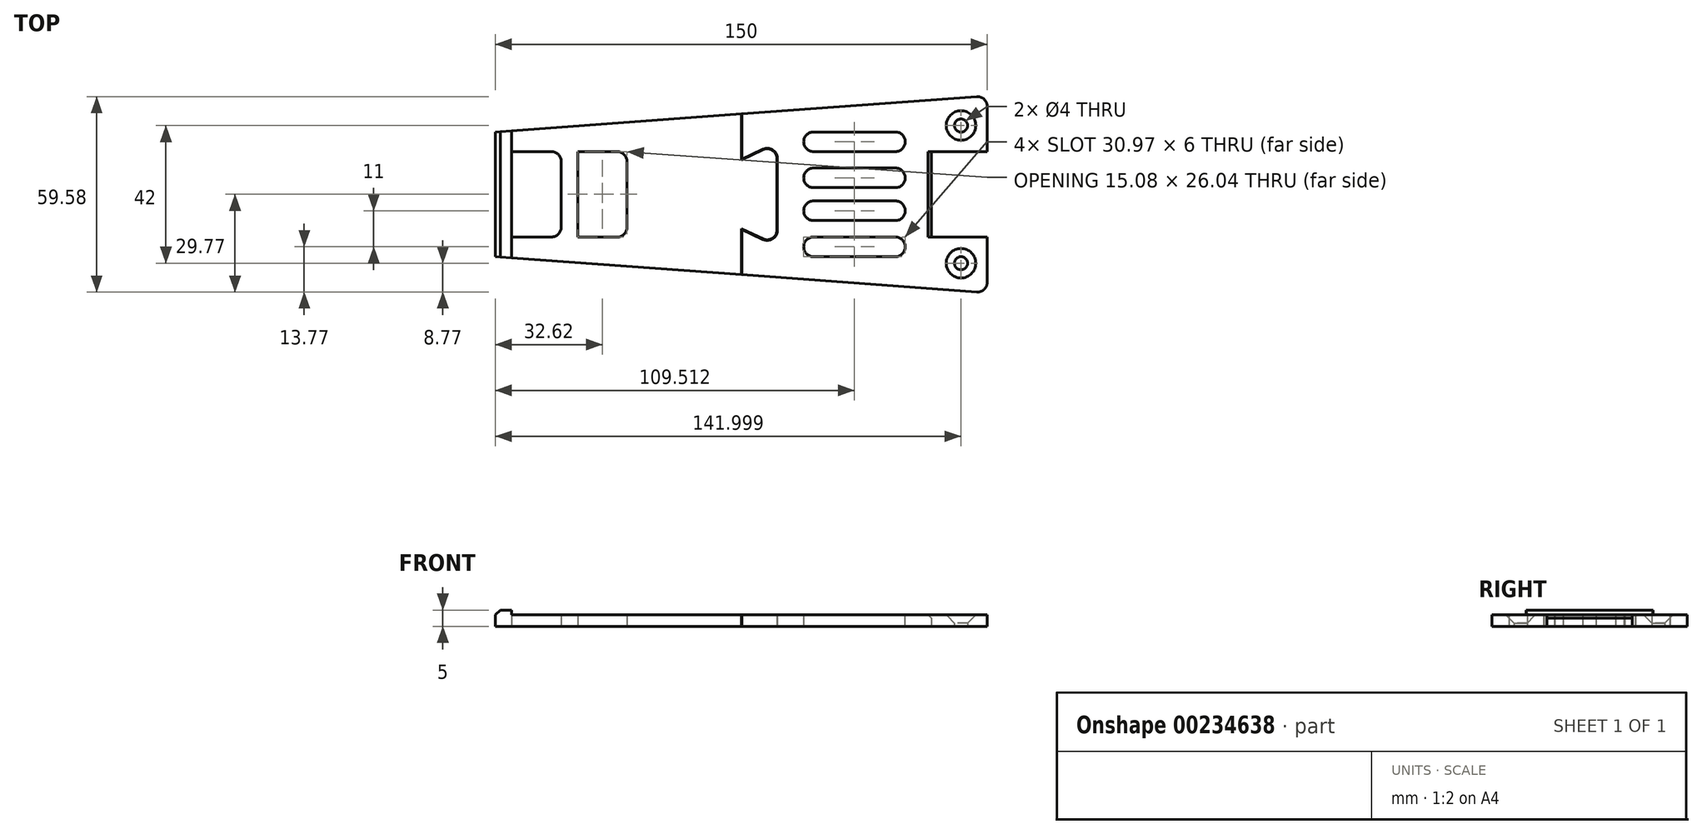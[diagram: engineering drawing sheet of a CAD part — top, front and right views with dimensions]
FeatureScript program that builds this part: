
annotation { "Feature Type Name" : "Feature", "Feature Type Description" : "" }
export const myFeature = defineFeature(function(context is Context, id is Id, definition is map)
    precondition{}
    {
        {
            var Q0;
            Q0=qCreatedBy(makeId("Top.planeOp"),FACE);
            var sketch = newSketch(context, id + "F0", { "sketchPlane" : qUnion([Q0])});
            skLineSegment(sketch, "E0.left", {"start": v(80.65, -28) * mm, "end": v(80.65, -11) * mm});
            skPoint(sketch, "E0.middle", {"position": v(0, 0) * mm});
            skLineSegment(sketch, "E1.trimOffspring", {"start": v(80.65, 15.04) * mm, "end": v(80.65, 32.04) * mm});
            skCircle(sketch, "E2", {"center": v(72.65, 23) * mm, "radius": 2 * mm});
            skCircle(sketch, "E3.MirrorC", {"center": v(72.65, -19) * mm, "radius": 2 * mm});
            skLineSegment(sketch, "E4", {"start": v(63.65, 15.04) * mm, "end": v(63.65, -11) * mm});
            skLineSegment(sketch, "E5", {"start": v(-49.27, -11) * mm, "end": v(-49.27, 15.04) * mm});
            skLineSegment(sketch, "E6", {"start": v(80.65, 15.04) * mm, "end": v(63.65, 15.04) * mm});
            skLineSegment(sketch, "E7", {"start": v(80.65, -11) * mm, "end": v(63.65, -11) * mm});
            skLineSegment(sketch, "E8", {"start": v(-49.27, 15.04) * mm, "end": v(-64.35, 15.04) * mm});
            skLineSegment(sketch, "E9", {"start": v(-49.27, -11) * mm, "end": v(-64.35, -11) * mm});
            skLineSegment(sketch, "E10", {"start": v(-64.35, -11) * mm, "end": v(-64.35, 15.04) * mm});
            skLineSegment(sketch, "E11", {"start": v(80.65, -28) * mm, "end": v(-69.35, -28) * mm, "construction": true});
            skLineSegment(sketch, "E12", {"start": v(80.65, 32.04) * mm, "end": v(-69.35, 32.04) * mm, "construction": true});
            skLineSegment(sketch, "E13", {"start": v(63.65, 15.04) * mm, "end": v(-49.27, 15.04) * mm, "construction": true});
            skLineSegment(sketch, "E14", {"start": v(-69.35, 32.04) * mm, "end": v(-69.35, 21.04) * mm, "construction": true});
            skLineSegment(sketch, "E15", {"start": v(-69.35, -28) * mm, "end": v(-69.35, -17) * mm, "construction": true});
            skLineSegment(sketch, "E16", {"start": v(-29.2, -11.02) * mm, "end": v(-29.2, 15.02) * mm});
            skLineSegment(sketch, "E17", {"start": v(-29.2, 15.02) * mm, "end": v(-44.27, 15.02) * mm});
            skLineSegment(sketch, "E18", {"start": v(-29.2, -11.02) * mm, "end": v(-44.27, -11.02) * mm});
            skLineSegment(sketch, "E19", {"start": v(-44.27, -11.02) * mm, "end": v(-44.27, 15.02) * mm});
            skLineSegment(sketch, "E20", {"start": v(80.65, 32.04) * mm, "end": v(5.8, 26.55) * mm});
            skLineSegment(sketch, "E21", {"start": v(80.65, -28) * mm, "end": v(5.8, -22.51) * mm});
            skLineSegment(sketch, "E22", {"start": v(-69.35, 21.04) * mm, "end": v(-69.35, -17) * mm});
            skLineSegment(sketch, "E23", {"start": v(5.65, 26.54) * mm, "end": v(5.65, 12.54) * mm});
            skLineSegment(sketch, "E24", {"start": v(5.65, -22.5) * mm, "end": v(5.65, -8.5) * mm});
            skLineSegment(sketch, "E25", {"start": v(5.65, -8.5) * mm, "end": v(12.26, -11.58) * mm});
            skLineSegment(sketch, "E26", {"start": v(16.52, -8.86) * mm, "end": v(16.52, 12.9) * mm});
            skLineSegment(sketch, "E27", {"start": v(5.65, 12.54) * mm, "end": v(12.26, 15.62) * mm});
            skLineSegment(sketch, "E28.trimOffspring", {"start": v(5.65, -8.5) * mm, "end": v(5.65, -22.5) * mm});
            skPoint(sketch, "E29.visualSharp", {"position": v(16.52, 17.6) * mm});
            skArc(sketch, "E29.filletArc", {"start": v(16.52, 12.9) * mm, "mid": v(15.14, 15.43) * mm, "end": v(12.26, 15.62) * mm});
            skPoint(sketch, "E30.visualSharp", {"position": v(16.52, -13.57) * mm});
            skArc(sketch, "E30.filletArc", {"start": v(12.26, -11.58) * mm, "mid": v(15.14, -11.4) * mm, "end": v(16.52, -8.86) * mm});
            skLineSegment(sketch, "E31.0", {"start": v(5.8, -22.51) * mm, "end": v(5.8, -8.74) * mm});
            skLineSegment(sketch, "E31.1", {"start": v(5.8, -8.74) * mm, "end": v(12.2, -11.72) * mm});
            skArc(sketch, "E31.2", {"start": v(12.2, -11.72) * mm, "mid": v(15.22, -11.52) * mm, "end": v(16.67, -8.86) * mm});
            skLineSegment(sketch, "E31.3", {"start": v(5.8, 26.55) * mm, "end": v(5.8, 12.77) * mm});
            skLineSegment(sketch, "E31.4", {"start": v(5.8, 12.77) * mm, "end": v(12.2, 15.75) * mm});
            skArc(sketch, "E31.5", {"start": v(16.67, 12.9) * mm, "mid": v(15.22, 15.56) * mm, "end": v(12.2, 15.75) * mm});
            skLineSegment(sketch, "E31.6", {"start": v(16.67, -8.86) * mm, "end": v(16.67, 12.9) * mm});
            skLineSegment(sketch, "E32.trimOffspring", {"start": v(5.65, -22.5) * mm, "end": v(-69.35, -17) * mm});
            skLineSegment(sketch, "E33.trimOffspring", {"start": v(5.65, 26.54) * mm, "end": v(-69.35, 21.04) * mm});
            skLineSegment(sketch, "E34", {"start": v(63.65, -11) * mm, "end": v(-49.27, -11) * mm, "construction": true});
            skLineSegment(sketch, "E35.bottom", {"start": v(24.67, -11) * mm, "end": v(55.65, -11) * mm});
            skLineSegment(sketch, "E35.top", {"start": v(24.67, -17) * mm, "end": v(55.65, -17) * mm});
            skLineSegment(sketch, "E35.left", {"start": v(24.67, -11) * mm, "end": v(24.67, -17) * mm});
            skLineSegment(sketch, "E35.right", {"start": v(55.65, -11) * mm, "end": v(55.65, -17) * mm});
            skLineSegment(sketch, "E36.bottom", {"start": v(24.67, 10.04) * mm, "end": v(55.65, 10.04) * mm});
            skLineSegment(sketch, "E36.top", {"start": v(24.67, 4.04) * mm, "end": v(55.65, 4.04) * mm});
            skLineSegment(sketch, "E36.left", {"start": v(24.67, 10.04) * mm, "end": v(24.67, 4.04) * mm});
            skLineSegment(sketch, "E36.right", {"start": v(55.65, 10.04) * mm, "end": v(55.65, 4.04) * mm});
            skLineSegment(sketch, "E37.bottom", {"start": v(24.67, 0) * mm, "end": v(55.65, 0) * mm});
            skLineSegment(sketch, "E37.top", {"start": v(24.67, -6) * mm, "end": v(55.65, -6) * mm});
            skLineSegment(sketch, "E37.left", {"start": v(24.67, 0) * mm, "end": v(24.67, -6) * mm});
            skLineSegment(sketch, "E37.right", {"start": v(55.65, 0) * mm, "end": v(55.65, -6) * mm});
            skLineSegment(sketch, "E38.bottom", {"start": v(24.67, 21.04) * mm, "end": v(55.65, 21.04) * mm});
            skLineSegment(sketch, "E38.top", {"start": v(24.67, 15.04) * mm, "end": v(55.65, 15.04) * mm});
            skLineSegment(sketch, "E38.left", {"start": v(24.67, 21.04) * mm, "end": v(24.67, 15.04) * mm});
            skLineSegment(sketch, "E38.right", {"start": v(55.65, 21.04) * mm, "end": v(55.65, 15.04) * mm});
            skSolve(sketch);
        }
        {
            var Q0;
            Q0=makeQuery(id+"F0.imprint","IMPRINT",FACE,{"disambiguationData":[TD([[makeQuery(id+"F0.imprint","IMPRINT",EDGE,{"derivedFrom":sQuery(id+"F0.wireOp",EDGE,"E5")}),-1.0]])]});
            var Q1;
            Q1=makeQuery(id+"F0.imprint","IMPRINT",FACE,{"disambiguationData":[TD([[makeQuery(id+"F0.imprint","IMPRINT",EDGE,{"derivedFrom":sQuery(id+"F0.wireOp",EDGE,"E0.left")}),1.0]])]});
            extrude(context, id + "F1", {"entities" : qUnion([Q0, Q1]), "depth" : 3.5 * mm});
        }
        {
            var Q0;
            {var subQ0=sQuery(id+"F0.wireOp",EDGE,"E4");Q0=makeQuery(id+"F1.opExtrude","CAP_EDGE",EDGE,{"disambiguationData":[OSD([subQ0]),TDD([makeQuery(id+"F0.imprint","IMPRINT",EDGE,{"disambiguationData":[TD([[makeQuery(id+"F0.imprint","INTERSECT",VERTEX,{"derivedFrom":[sQuery(id+"F0.wireOp",EDGE,"a1183fda-915b-4a70-979b-ef1662e096630.MirrorCS"),subQ0]}),-1.0]])],"derivedFrom":subQ0})])],"isStart":false});}
            var Q1;
            {var subQ0=sQuery(id+"F0.wireOp",EDGE,"E4");Q1=makeQuery(id+"F1.opExtrude","CAP_EDGE",EDGE,{"disambiguationData":[OSD([subQ0]),TDD([makeQuery(id+"F0.imprint","IMPRINT",EDGE,{"disambiguationData":[TD([[makeQuery(id+"F0.imprint","INTERSECT",VERTEX,{"derivedFrom":[sQuery(id+"F0.wireOp",EDGE,"irKfdA7U-XoDH-ahAc-nykv-EBvfS3rGnkAg.top"),subQ0]}),1.0]])],"derivedFrom":subQ0})])],"isStart":false});}
            chamfer(context, id + "F2", {"entities" : qUnion([Q0, Q1]), "width" : 1 * mm, "tangentPropagation" : true});
        }
        {
            var Q0;
            Q0=makeQuery(id+"F1.opExtrude","CAP_EDGE",EDGE,{"disambiguationData":[OSD([sQuery(id+"F0.wireOp",EDGE,"E2")])],"isStart":false});
            var Q1;
            Q1=makeQuery(id+"F1.opExtrude","CAP_EDGE",EDGE,{"disambiguationData":[OSD([sQuery(id+"F0.wireOp",EDGE,"E3.MirrorC")])],"isStart":false});
            chamfer(context, id + "F3", {"entities" : qUnion([Q0, Q1]), "width" : 2.5 * mm, "tangentPropagation" : true});
        }
        {
            var Q0;
            Q0=makeQuery(id+"F1.opExtrude","CAP_FACE",FACE,{"disambiguationData":[OSD([sQuery(id+"F0.wireOp",EDGE,"E5"),sQuery(id+"F0.wireOp",EDGE,"E8"),sQuery(id+"F0.wireOp",EDGE,"E9"),sQuery(id+"F0.wireOp",EDGE,"E10"),sQuery(id+"F0.wireOp",EDGE,"E16"),sQuery(id+"F0.wireOp",EDGE,"E17"),sQuery(id+"F0.wireOp",EDGE,"E18"),sQuery(id+"F0.wireOp",EDGE,"E19"),sQuery(id+"F0.wireOp",EDGE,"E22"),sQuery(id+"F0.wireOp",EDGE,"E25"),sQuery(id+"F0.wireOp",EDGE,"E26"),sQuery(id+"F0.wireOp",EDGE,"E23"),sQuery(id+"F0.wireOp",EDGE,"E27"),sQuery(id+"F0.wireOp",EDGE,"E28.trimOffspring"),sQuery(id+"F0.wireOp",EDGE,"E29.filletArc"),sQuery(id+"F0.wireOp",EDGE,"E30.filletArc"),sQuery(id+"F0.wireOp",EDGE,"E32.trimOffspring"),sQuery(id+"F0.wireOp",EDGE,"E33.trimOffspring")])],"isStart":false});
            var sketch = newSketch(context, id + "F4", { "sketchPlane" : qUnion([Q0])});
            skLineSegment(sketch, "E39", {"start": v(-69.35, 21.04) * mm, "end": v(-69.35, -17) * mm});
            skLineSegment(sketch, "E40", {"start": v(-69.35, -17) * mm, "end": v(-64.35, -17.37) * mm});
            skLineSegment(sketch, "E41", {"start": v(-64.35, -17.37) * mm, "end": v(-64.35, 21.4) * mm});
            skLineSegment(sketch, "E42", {"start": v(-64.35, 21.4) * mm, "end": v(-69.35, 21.04) * mm});
            skLineSegment(sketch, "E43", {"start": v(-49.27, 22.5) * mm, "end": v(-49.27, -18.47) * mm});
            skLineSegment(sketch, "E44", {"start": v(-49.27, -18.47) * mm, "end": v(-44.27, -18.84) * mm});
            skLineSegment(sketch, "E45", {"start": v(-44.27, -18.84) * mm, "end": v(-44.27, 22.88) * mm});
            skLineSegment(sketch, "E46", {"start": v(-44.27, 22.88) * mm, "end": v(-49.27, 22.5) * mm});
            skSolve(sketch);
        }
        {
            var Q0;
            Q0=makeQuery(id+"F4.imprint","IMPRINT",FACE,{"disambiguationData":[TD([[makeQuery(id+"F4.imprint","IMPRINT",EDGE,{"derivedFrom":sQuery(id+"F4.wireOp",EDGE,"E39")}),1.0]])]});
            var Q1;
            {var subQ0=sQuery(id+"F4.wireOp",EDGE,"E44");Q1=makeQuery(id+"F4.imprint","IMPRINT",FACE,{"disambiguationData":[TD([[makeQuery(id+"F4.imprint","IMPRINT",EDGE,{"derivedFrom":subQ0}),-1.0]])]});}
            extrude(context, id + "F5", {"entities" : qUnion([Q0, Q1]), "operationType" : NewBodyOperationType.ADD, "depth" : 1.5 * mm});
        }
        {
            var Q0;
            Q0=makeQuery(id+"F1.opExtrude","SWEPT_EDGE",EDGE,{"disambiguationData":[OSD([sQuery(id+"F0.wireOp",EDGE,"E5"),sQuery(id+"F0.wireOp",EDGE,"E8")])]});
            var Q1;
            Q1=makeQuery(id+"F1.opExtrude","SWEPT_EDGE",EDGE,{"disambiguationData":[OSD([sQuery(id+"F0.wireOp",EDGE,"E16"),sQuery(id+"F0.wireOp",EDGE,"E17")])]});
            var Q2;
            Q2=makeQuery(id+"F1.opExtrude","SWEPT_EDGE",EDGE,{"disambiguationData":[OSD([sQuery(id+"F0.wireOp",EDGE,"E5"),sQuery(id+"F0.wireOp",EDGE,"E9")])]});
            var Q3;
            Q3=makeQuery(id+"F1.opExtrude","SWEPT_EDGE",EDGE,{"disambiguationData":[OSD([sQuery(id+"F0.wireOp",EDGE,"E16"),sQuery(id+"F0.wireOp",EDGE,"E18")])]});
            fillet(context, id + "F6", {"entities" : qUnion([Q0, Q1, Q2, Q3]), "radius" : 3 * mm, "tangentPropagation" : true, "allowEdgeOverflow" : false});
        }
        {
            var Q0;
            Q0=makeQuery(id+"F5.opExtrude","CAP_EDGE",EDGE,{"disambiguationData":[OSD([sQuery(id+"F4.wireOp",EDGE,"E39")])],"isStart":false});
            var Q1;
            Q1=makeQuery(id+"F5.opExtrude","CAP_EDGE",EDGE,{"disambiguationData":[OSD([sQuery(id+"F4.wireOp",EDGE,"E43")])],"isStart":false});
            chamfer(context, id + "F7", {"entities" : qUnion([Q0, Q1]), "width" : 1.5 * mm, "tangentPropagation" : true});
        }
        {
            var Q0;
            Q0=makeQuery(id+"F1.opExtrude","SWEPT_EDGE",EDGE,{"disambiguationData":[OSD([sQuery(id+"F0.wireOp",EDGE,"E1.trimOffspring"),sQuery(id+"F0.wireOp",EDGE,"E20")])]});
            var Q1;
            Q1=makeQuery(id+"F1.opExtrude","SWEPT_EDGE",EDGE,{"disambiguationData":[OSD([sQuery(id+"F0.wireOp",EDGE,"E0.left"),sQuery(id+"F0.wireOp",EDGE,"E21")])]});
            fillet(context, id + "F8", {"entities" : qUnion([Q0, Q1]), "radius" : 3 * mm, "tangentPropagation" : true, "allowEdgeOverflow" : false});
        }
        {
            var Q0;
            Q0=makeQuery(id+"F1.opExtrude","SWEPT_EDGE",EDGE,{"disambiguationData":[OSD([sQuery(id+"F0.wireOp",EDGE,"E38.bottom"),sQuery(id+"F0.wireOp",EDGE,"E38.left")])]});
            var Q1;
            Q1=makeQuery(id+"F1.opExtrude","SWEPT_EDGE",EDGE,{"disambiguationData":[OSD([sQuery(id+"F0.wireOp",EDGE,"E36.bottom"),sQuery(id+"F0.wireOp",EDGE,"E36.left")])]});
            var Q2;
            Q2=makeQuery(id+"F1.opExtrude","SWEPT_EDGE",EDGE,{"disambiguationData":[OSD([sQuery(id+"F0.wireOp",EDGE,"E37.bottom"),sQuery(id+"F0.wireOp",EDGE,"E37.left")])]});
            var Q3;
            Q3=makeQuery(id+"F1.opExtrude","SWEPT_EDGE",EDGE,{"disambiguationData":[OSD([sQuery(id+"F0.wireOp",EDGE,"E35.bottom"),sQuery(id+"F0.wireOp",EDGE,"E35.left")])]});
            var Q4;
            Q4=makeQuery(id+"F1.opExtrude","SWEPT_EDGE",EDGE,{"disambiguationData":[OSD([sQuery(id+"F0.wireOp",EDGE,"E38.top"),sQuery(id+"F0.wireOp",EDGE,"E38.left")])]});
            var Q5;
            Q5=makeQuery(id+"F1.opExtrude","SWEPT_EDGE",EDGE,{"disambiguationData":[OSD([sQuery(id+"F0.wireOp",EDGE,"E36.top"),sQuery(id+"F0.wireOp",EDGE,"E36.left")])]});
            var Q6;
            Q6=makeQuery(id+"F1.opExtrude","SWEPT_EDGE",EDGE,{"disambiguationData":[OSD([sQuery(id+"F0.wireOp",EDGE,"E37.top"),sQuery(id+"F0.wireOp",EDGE,"E37.left")])]});
            var Q7;
            Q7=makeQuery(id+"F1.opExtrude","SWEPT_EDGE",EDGE,{"disambiguationData":[OSD([sQuery(id+"F0.wireOp",EDGE,"E35.top"),sQuery(id+"F0.wireOp",EDGE,"E35.left")])]});
            var Q8;
            Q8=makeQuery(id+"F1.opExtrude","SWEPT_EDGE",EDGE,{"disambiguationData":[OSD([sQuery(id+"F0.wireOp",EDGE,"E38.bottom"),sQuery(id+"F0.wireOp",EDGE,"E38.right")])]});
            var Q9;
            Q9=makeQuery(id+"F1.opExtrude","SWEPT_EDGE",EDGE,{"disambiguationData":[OSD([sQuery(id+"F0.wireOp",EDGE,"E36.bottom"),sQuery(id+"F0.wireOp",EDGE,"E36.right")])]});
            var Q10;
            Q10=makeQuery(id+"F1.opExtrude","SWEPT_EDGE",EDGE,{"disambiguationData":[OSD([sQuery(id+"F0.wireOp",EDGE,"E37.bottom"),sQuery(id+"F0.wireOp",EDGE,"E37.right")])]});
            var Q11;
            Q11=makeQuery(id+"F1.opExtrude","SWEPT_EDGE",EDGE,{"disambiguationData":[OSD([sQuery(id+"F0.wireOp",EDGE,"E35.bottom"),sQuery(id+"F0.wireOp",EDGE,"E35.right")])]});
            var Q12;
            Q12=makeQuery(id+"F1.opExtrude","SWEPT_EDGE",EDGE,{"disambiguationData":[OSD([sQuery(id+"F0.wireOp",EDGE,"E35.top"),sQuery(id+"F0.wireOp",EDGE,"E35.right")])]});
            var Q13;
            Q13=makeQuery(id+"F1.opExtrude","SWEPT_EDGE",EDGE,{"disambiguationData":[OSD([sQuery(id+"F0.wireOp",EDGE,"E37.top"),sQuery(id+"F0.wireOp",EDGE,"E37.right")])]});
            var Q14;
            Q14=makeQuery(id+"F1.opExtrude","SWEPT_EDGE",EDGE,{"disambiguationData":[OSD([sQuery(id+"F0.wireOp",EDGE,"E36.top"),sQuery(id+"F0.wireOp",EDGE,"E36.right")])]});
            var Q15;
            Q15=makeQuery(id+"F1.opExtrude","SWEPT_EDGE",EDGE,{"disambiguationData":[OSD([sQuery(id+"F0.wireOp",EDGE,"E38.top"),sQuery(id+"F0.wireOp",EDGE,"E38.right")])]});
            fillet(context, id + "F9", {"entities" : qUnion([Q0, Q1, Q2, Q3, Q4, Q5, Q6, Q7, Q8, Q9, Q10, Q11, Q12, Q13, Q14, Q15]), "radius" : 3 * mm, "tangentPropagation" : true, "allowEdgeOverflow" : false});
        }
    });
